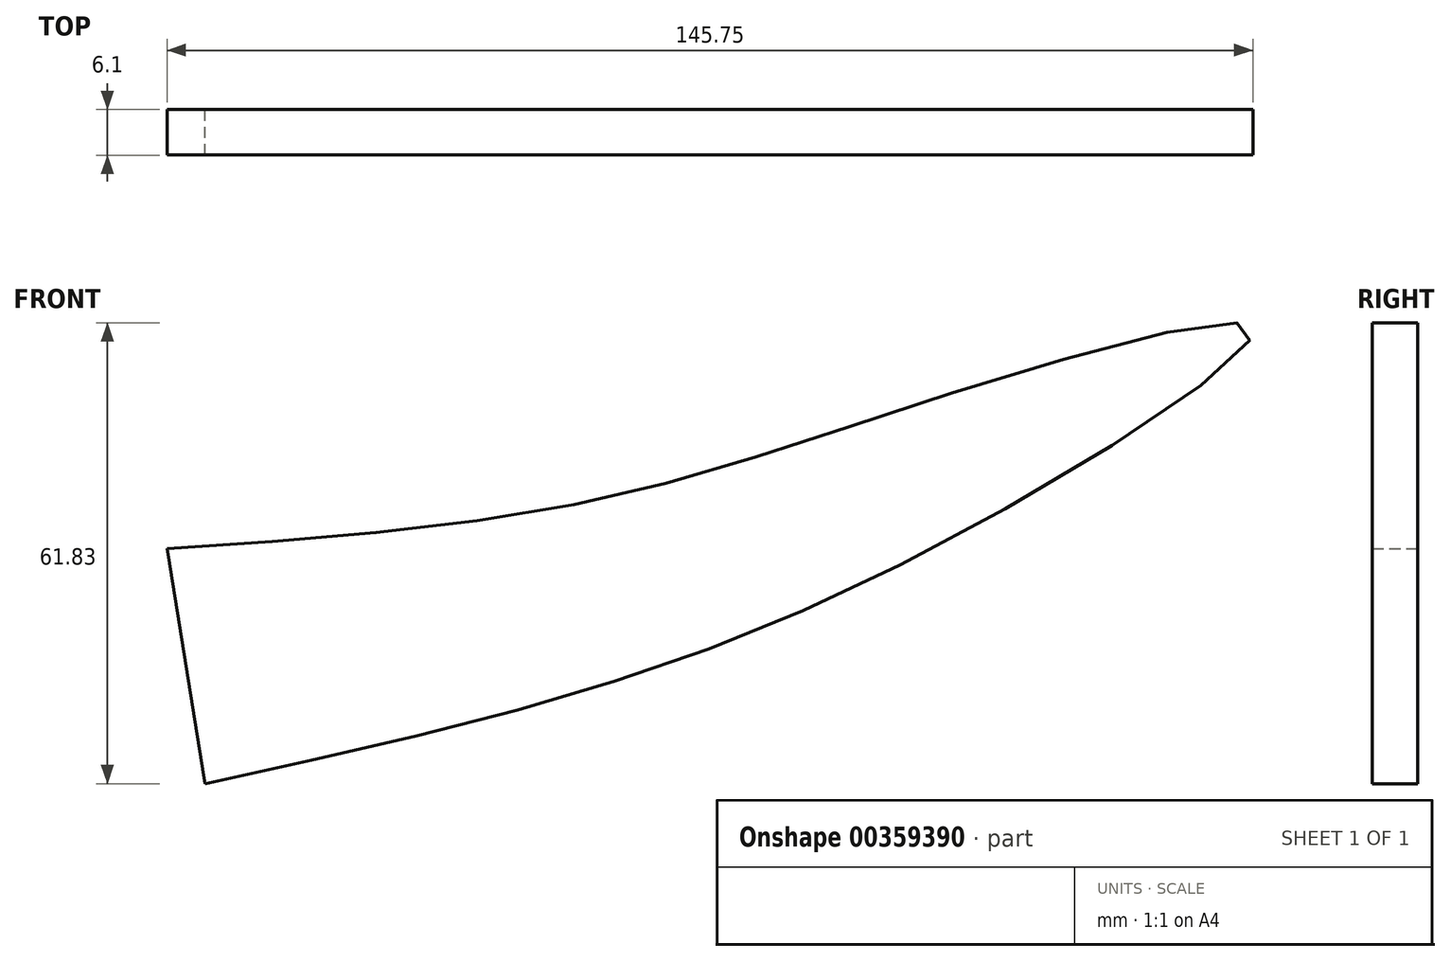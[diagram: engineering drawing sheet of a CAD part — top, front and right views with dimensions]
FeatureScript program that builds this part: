
annotation { "Feature Type Name" : "Feature", "Feature Type Description" : "" }
export const myFeature = defineFeature(function(context is Context, id is Id, definition is map)
    precondition{}
    {
        {
            var Q0;
            Q0=qCreatedBy(makeId("Front.planeOp"),FACE);
            var sketch = newSketch(context, id + "F0", { "sketchPlane" : qUnion([Q0])});
            skFitSpline(sketch, "E0", {"points": [v(0, 23.9) * mm, v(56.11, 30.1) * mm, v(107.08, 45.32) * mm, v(145.69, 53.38) * mm, v(109.14, 27.39) * mm, v(54.05, 4.28) * mm, v(-6.18, -10.02) * mm], "startDerivative": vector(336.63, 22.77) * mm, "endDerivative": vector(-343.25, -72.55) * mm});
            skLineSegment(sketch, "E1", {"start": v(0, 23.9) * mm, "end": v(5.11, -7.62) * mm});
            skSolve(sketch);
        }
        {
            var Q0;
            Q0 = qSketchRegion(id + "F0", true);
            extrude(context, id + "F1", {"entities" : qUnion([Q0]), "depth" : 6.1 * mm});
        }
    });
